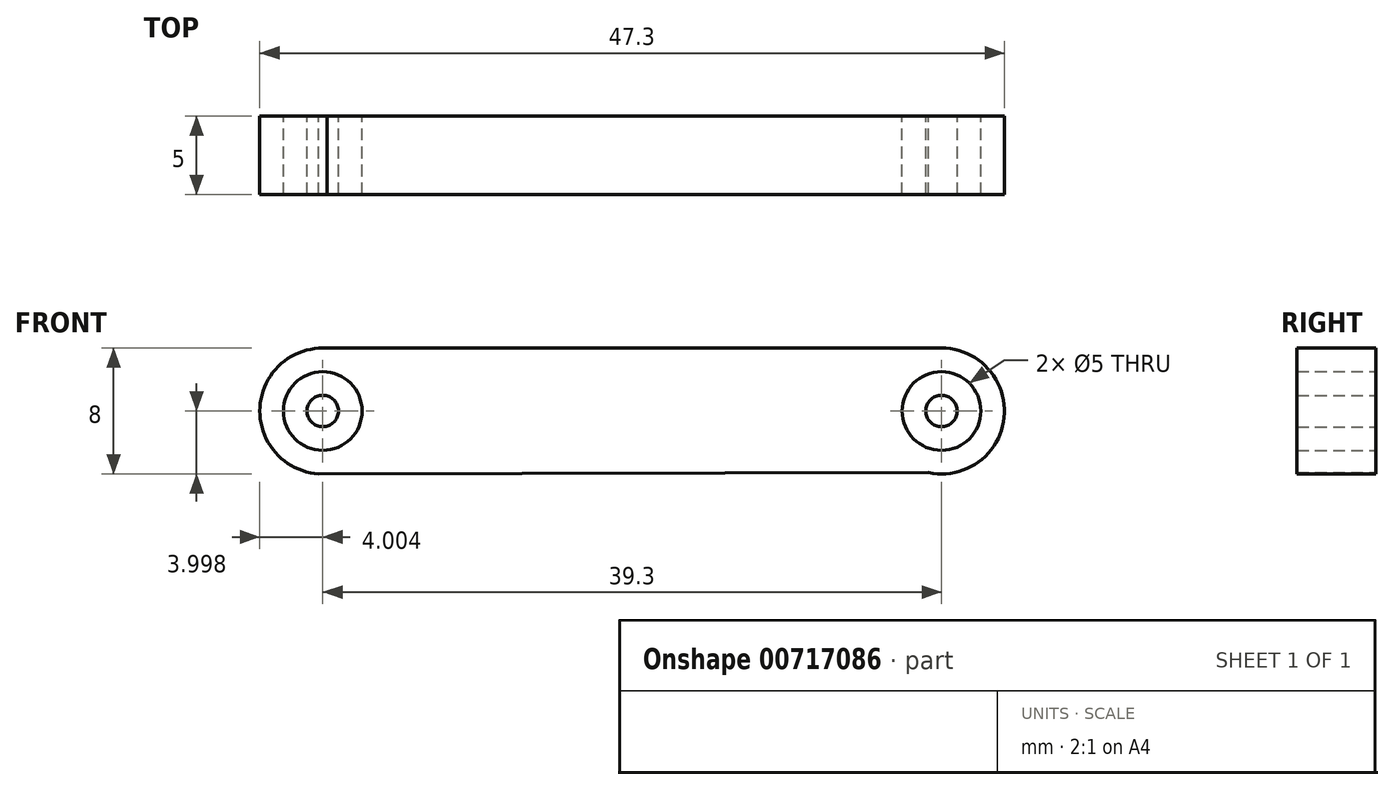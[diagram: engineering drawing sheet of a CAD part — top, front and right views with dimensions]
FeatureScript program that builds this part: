
annotation { "Feature Type Name" : "Feature", "Feature Type Description" : "" }
export const myFeature = defineFeature(function(context is Context, id is Id, definition is map)
    precondition{}
    {
        {
            var Q0;
            Q0=qCreatedBy(makeId("Front.planeOp"),FACE);
            var sketch = newSketch(context, id + "F0", { "sketchPlane" : qUnion([Q0])});
            skLineSegment(sketch, "E0", {"start": v(-19.37, 22.09) * mm, "end": v(19.93, 22.09) * mm});
            skCircle(sketch, "E1", {"center": v(-19.37, 22.09) * mm, "radius": 2.5 * mm});
            skArc(sketch, "E2", {"start": v(-19.1, 26.08) * mm, "mid": v(-23.37, 22.08) * mm, "end": v(-19.09, 18.1) * mm});
            skCircle(sketch, "E3", {"center": v(19.93, 22.09) * mm, "radius": 2.5 * mm});
            skArc(sketch, "E4", {"start": v(19.11, 18.17) * mm, "mid": v(23.91, 21.67) * mm, "end": v(19.93, 26.09) * mm});
            skCircle(sketch, "E5", {"center": v(-19.37, 22.09) * mm, "radius": 1 * mm});
            skCircle(sketch, "E6", {"center": v(19.93, 22.09) * mm, "radius": 1 * mm});
            skLineSegment(sketch, "E7", {"start": v(-19.63, 18.1) * mm, "end": v(19.11, 18.17) * mm});
            skLineSegment(sketch, "E8", {"start": v(-19.1, 26.08) * mm, "end": v(19.93, 26.09) * mm});
            skSolve(sketch);
        }
        {
            var Q0;
            Q0=makeQuery(id+"F0.imprint","IMPRINT",FACE,{"disambiguationData":[TD([[makeQuery(id+"F0.imprint","IMPRINT",EDGE,{"derivedFrom":sQuery(id+"F0.wireOp",EDGE,"E1")}),-1.0]])]});
            extrude(context, id + "F1", {"entities" : qUnion([Q0]), "depth" : 5 * mm, "offsetDistance" : 25.4 * mm});
        }
        {
            var Q0;
            Q0=makeQuery(id+"F0.imprint","IMPRINT",FACE,{"disambiguationData":[TD([[makeQuery(id+"F0.imprint","IMPRINT",EDGE,{"derivedFrom":sQuery(id+"F0.wireOp",EDGE,"E5")}),1.0]])]});
            var Q1;
            Q1=makeQuery(id+"F0.imprint","IMPRINT",FACE,{"disambiguationData":[TD([[makeQuery(id+"F0.imprint","IMPRINT",EDGE,{"derivedFrom":sQuery(id+"F0.wireOp",EDGE,"E6")}),1.0]])]});
            extrude(context, id + "F2", {"entities" : qUnion([Q0, Q1]), "depth" : 5 * mm, "offsetDistance" : 25.4 * mm});
        }
    });
